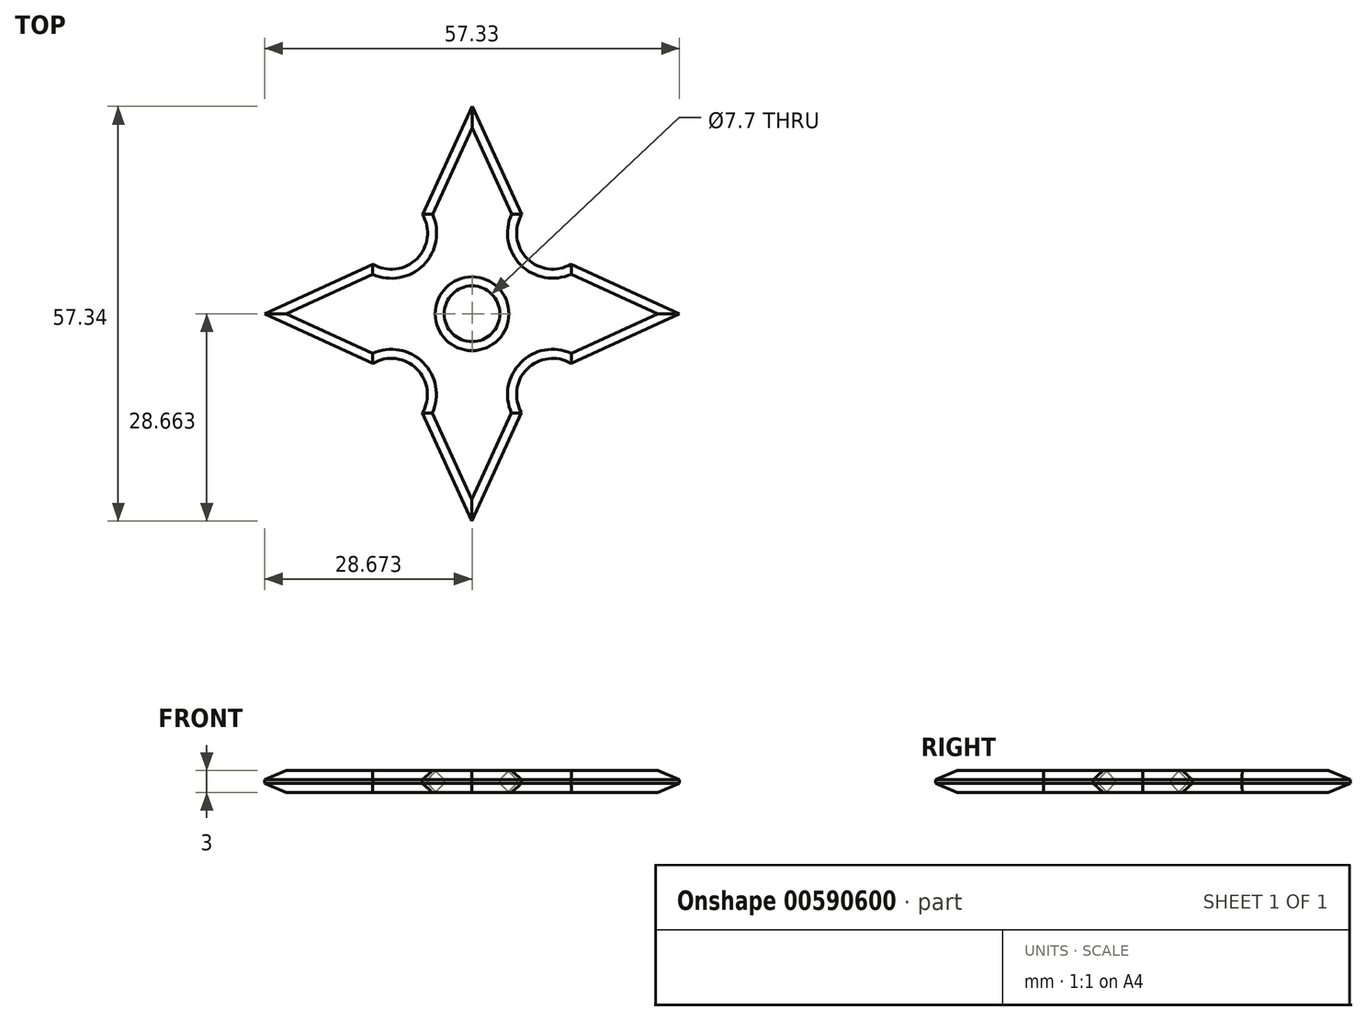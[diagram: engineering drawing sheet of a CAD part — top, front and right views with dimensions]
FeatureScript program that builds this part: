
annotation { "Feature Type Name" : "Feature", "Feature Type Description" : "" }
export const myFeature = defineFeature(function(context is Context, id is Id, definition is map)
    precondition{}
    {
        {
            var Q0;
            Q0=qCreatedBy(makeId("Top.planeOp"),FACE);
            var sketch = newSketch(context, id + "F0", { "sketchPlane" : qUnion([Q0])});
            skLineSegment(sketch, "E0", {"start": v(-25.6, 18.45) * mm, "end": v(-25.6, 33.4) * mm});
            skLineSegment(sketch, "E1", {"start": v(-39.32, 4.73) * mm, "end": v(-54.28, 4.73) * mm});
            skLineSegment(sketch, "E2", {"start": v(-25.62, -8.97) * mm, "end": v(-25.62, -23.93) * mm});
            skLineSegment(sketch, "E3", {"start": v(-11.91, 4.73) * mm, "end": v(3.05, 4.73) * mm});
            skLineSegment(sketch, "E4", {"start": v(-25.6, 33.4) * mm, "end": v(-32.46, 18.45) * mm});
            skLineSegment(sketch, "E5", {"start": v(-32.46, 18.45) * mm, "end": v(-25.6, 33.4) * mm});
            skLineSegment(sketch, "E6", {"start": v(-25.6, 33.4) * mm, "end": v(-18.75, 18.45) * mm});
            skLineSegment(sketch, "E7", {"start": v(-11.9, 11.6) * mm, "end": v(3.05, 4.73) * mm});
            skLineSegment(sketch, "E8", {"start": v(3.05, 4.73) * mm, "end": v(-11.91, -2.13) * mm});
            skLineSegment(sketch, "E9", {"start": v(-25.62, -23.93) * mm, "end": v(-32.48, -8.97) * mm});
            skLineSegment(sketch, "E10", {"start": v(-18.76, -8.97) * mm, "end": v(-25.62, -23.93) * mm});
            skLineSegment(sketch, "E11", {"start": v(-39.32, 11.6) * mm, "end": v(-54.28, 4.73) * mm});
            skLineSegment(sketch, "E12", {"start": v(-54.28, 4.73) * mm, "end": v(-39.32, -2.12) * mm});
            skLineSegment(sketch, "E13", {"start": v(-32.46, 18.45) * mm, "end": v(-18.75, 18.45) * mm});
            skLineSegment(sketch, "E14", {"start": v(-11.9, 11.6) * mm, "end": v(-11.91, -2.13) * mm});
            skLineSegment(sketch, "E15", {"start": v(-18.76, -8.97) * mm, "end": v(-32.48, -8.97) * mm});
            skLineSegment(sketch, "E16", {"start": v(-39.32, -2.12) * mm, "end": v(-39.32, 11.6) * mm});
            skLineSegment(sketch, "E17", {"start": v(-32.48, -8.97) * mm, "end": v(-18.76, -8.97) * mm});
            skLineSegment(sketch, "E18", {"start": v(-11.91, -2.13) * mm, "end": v(-11.9, 11.6) * mm});
            skArc(sketch, "E19", {"start": v(-39.32, 11.6) * mm, "mid": v(-33.22, 12.35) * mm, "end": v(-32.46, 18.45) * mm});
            skArc(sketch, "E20", {"start": v(-11.91, -2.13) * mm, "mid": v(-17.98, -2.9) * mm, "end": v(-18.76, -8.97) * mm});
            skArc(sketch, "E21", {"start": v(-32.48, -8.97) * mm, "mid": v(-33.25, -2.9) * mm, "end": v(-39.32, -2.12) * mm});
            skArc(sketch, "E22", {"start": v(-18.75, 18.45) * mm, "mid": v(-17.98, 12.36) * mm, "end": v(-11.9, 11.6) * mm});
            skCircle(sketch, "E23", {"center": v(-25.6, 4.73) * mm, "radius": 3.85 * mm});
            skLineSegment(sketch, "E24", {"start": v(-25.6, 33.4) * mm, "end": v(-54.28, 33.4) * mm});
            skLineSegment(sketch, "E25", {"start": v(-54.28, 33.4) * mm, "end": v(-54.28, -23.93) * mm});
            skLineSegment(sketch, "E26", {"start": v(-54.28, -23.93) * mm, "end": v(3.05, -23.93) * mm});
            skLineSegment(sketch, "E27", {"start": v(3.05, -23.93) * mm, "end": v(3.05, 33.4) * mm});
            skLineSegment(sketch, "E28", {"start": v(3.05, 33.4) * mm, "end": v(-25.6, 33.4) * mm});
            skSolve(sketch);
        }
        {
            var Q0;
            {var subQ1=sQuery(id+"F0.wireOp",EDGE,"E19");Q0=makeQuery(id+"F0.imprint","IMPRINT",FACE,{"disambiguationData":[TD([[makeQuery(id+"F0.imprint","IMPRINT",EDGE,{"derivedFrom":subQ1}),-1.0]])]});}
            var Q1;
            {var subQ0=sQuery(id+"F0.wireOp",EDGE,"E0");Q1=makeQuery(id+"F0.imprint","IMPRINT",FACE,{"disambiguationData":[TD([[makeQuery(id+"F0.imprint","IMPRINT",EDGE,{"derivedFrom":subQ0}),1.0]])]});}
            var Q2;
            {var subQ0=sQuery(id+"F0.wireOp",EDGE,"E0");Q2=makeQuery(id+"F0.imprint","IMPRINT",FACE,{"disambiguationData":[TD([[makeQuery(id+"F0.imprint","IMPRINT",EDGE,{"derivedFrom":subQ0}),-1.0]])]});}
            var Q3;
            {var subQ0=sQuery(id+"F0.wireOp",EDGE,"E1");Q3=makeQuery(id+"F0.imprint","IMPRINT",FACE,{"disambiguationData":[TD([[makeQuery(id+"F0.imprint","IMPRINT",EDGE,{"derivedFrom":subQ0}),-1.0]])]});}
            var Q4;
            {var subQ0=sQuery(id+"F0.wireOp",EDGE,"E1");Q4=makeQuery(id+"F0.imprint","IMPRINT",FACE,{"disambiguationData":[TD([[makeQuery(id+"F0.imprint","IMPRINT",EDGE,{"derivedFrom":subQ0}),1.0]])]});}
            var Q5;
            {var subQ0=sQuery(id+"F0.wireOp",EDGE,"E7");Q5=makeQuery(id+"F0.imprint","IMPRINT",FACE,{"disambiguationData":[TD([[makeQuery(id+"F0.imprint","IMPRINT",EDGE,{"derivedFrom":subQ0}),-1.0]])]});}
            var Q6;
            {var subQ0=sQuery(id+"F0.wireOp",EDGE,"E8");Q6=makeQuery(id+"F0.imprint","IMPRINT",FACE,{"disambiguationData":[TD([[makeQuery(id+"F0.imprint","IMPRINT",EDGE,{"derivedFrom":subQ0}),-1.0]])]});}
            var Q7;
            {var subQ0=sQuery(id+"F0.wireOp",EDGE,"E2");Q7=makeQuery(id+"F0.imprint","IMPRINT",FACE,{"disambiguationData":[TD([[makeQuery(id+"F0.imprint","IMPRINT",EDGE,{"derivedFrom":subQ0}),-1.0]])]});}
            var Q8;
            {var subQ0=sQuery(id+"F0.wireOp",EDGE,"E2");Q8=makeQuery(id+"F0.imprint","IMPRINT",FACE,{"disambiguationData":[TD([[makeQuery(id+"F0.imprint","IMPRINT",EDGE,{"derivedFrom":subQ0}),1.0]])]});}
            extrude(context, id + "F1", {"entities" : qUnion([Q0, Q1, Q2, Q3, Q4, Q5, Q6, Q7, Q8]), "depth" : 3 * mm, "offsetDistance" : 25 * mm});
        }
        {
            var Q0;
            Q0=makeQuery(id+"F1.opExtrude","CAP_FACE",FACE,{"disambiguationData":[OSD([sQuery(id+"F0.wireOp",EDGE,"E5"),sQuery(id+"F0.wireOp",EDGE,"E6"),sQuery(id+"F0.wireOp",EDGE,"E7"),sQuery(id+"F0.wireOp",EDGE,"E8"),sQuery(id+"F0.wireOp",EDGE,"E9"),sQuery(id+"F0.wireOp",EDGE,"E10"),sQuery(id+"F0.wireOp",EDGE,"E11"),sQuery(id+"F0.wireOp",EDGE,"E12"),sQuery(id+"F0.wireOp",EDGE,"E19"),sQuery(id+"F0.wireOp",EDGE,"E20"),sQuery(id+"F0.wireOp",EDGE,"E21"),sQuery(id+"F0.wireOp",EDGE,"E22"),sQuery(id+"F0.wireOp",EDGE,"E23")])],"isStart":false});
            var Q1;
            Q1=makeQuery(id+"F1.opExtrude","CAP_FACE",FACE,{"disambiguationData":[OSD([sQuery(id+"F0.wireOp",EDGE,"E5"),sQuery(id+"F0.wireOp",EDGE,"E6"),sQuery(id+"F0.wireOp",EDGE,"E7"),sQuery(id+"F0.wireOp",EDGE,"E8"),sQuery(id+"F0.wireOp",EDGE,"E9"),sQuery(id+"F0.wireOp",EDGE,"E10"),sQuery(id+"F0.wireOp",EDGE,"E11"),sQuery(id+"F0.wireOp",EDGE,"E12"),sQuery(id+"F0.wireOp",EDGE,"E19"),sQuery(id+"F0.wireOp",EDGE,"E20"),sQuery(id+"F0.wireOp",EDGE,"E21"),sQuery(id+"F0.wireOp",EDGE,"E22"),sQuery(id+"F0.wireOp",EDGE,"E23")])],"isStart":true});
            chamfer(context, id + "F2", {"entities" : qUnion([Q0, Q1]), "width" : 1.25 * mm, "tangentPropagation" : true});
        }
    });
